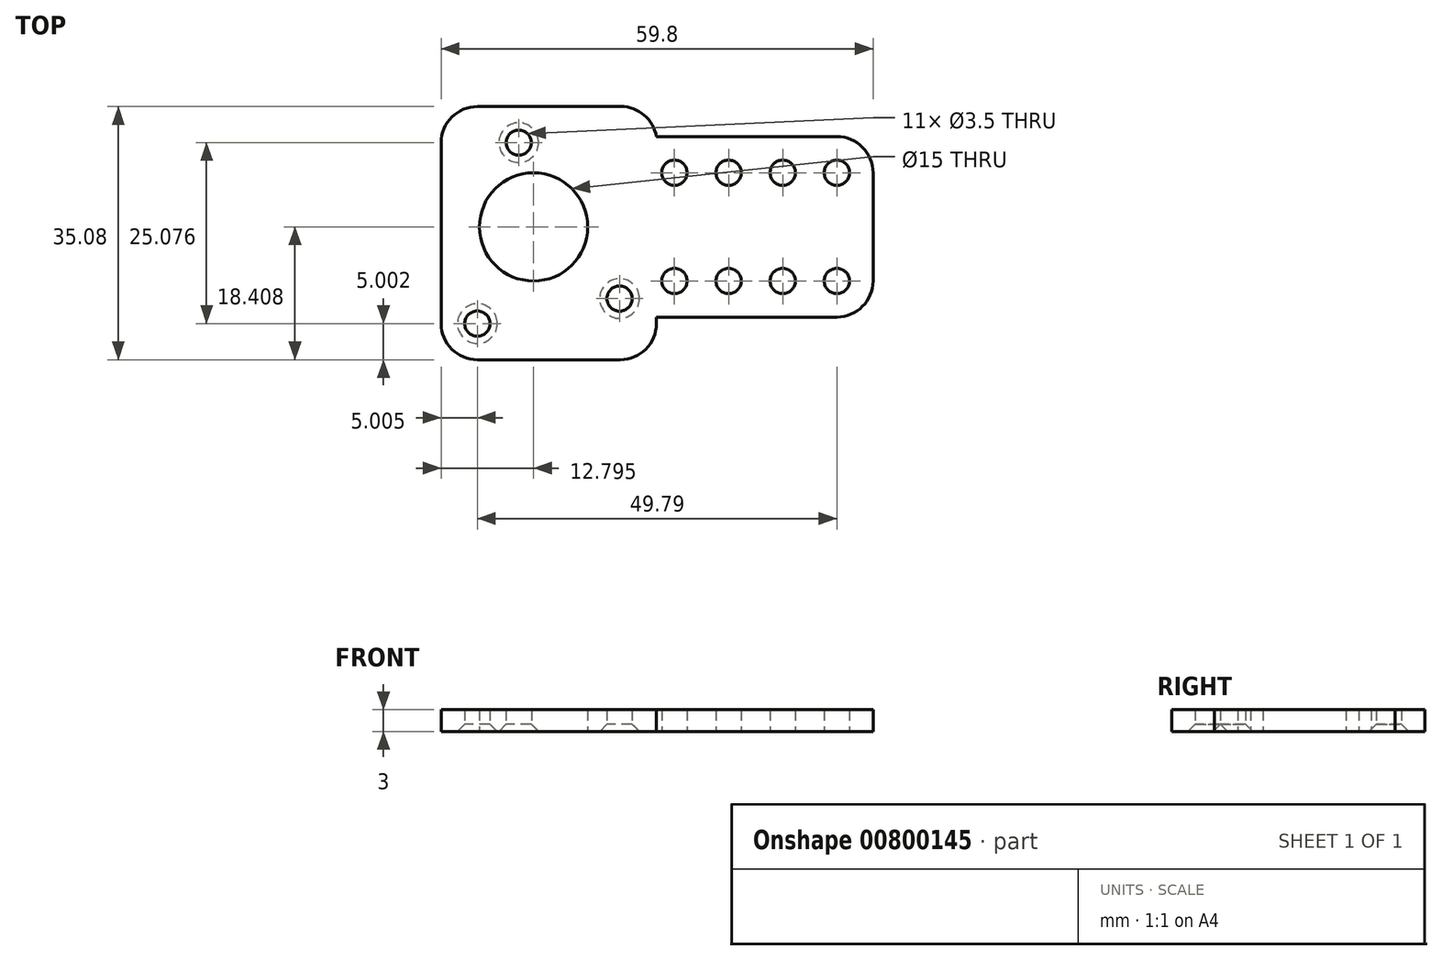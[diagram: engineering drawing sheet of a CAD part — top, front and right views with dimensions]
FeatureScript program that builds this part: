
annotation { "Feature Type Name" : "Feature", "Feature Type Description" : "" }
export const myFeature = defineFeature(function(context is Context, id is Id, definition is map)
    precondition{}
    {
        {
            var Q0;
            Q0=qCreatedBy(makeId("Top.planeOp"),FACE);
            var sketch = newSketch(context, id + "F0", { "sketchPlane" : qUnion([Q0])});
            skLineSegment(sketch, "E0.bottom", {"start": v(-29.9, 17.54) * mm, "end": v(29.9, 17.54) * mm});
            skLineSegment(sketch, "E0.top", {"start": v(-29.9, -17.54) * mm, "end": v(29.9, -17.54) * mm});
            skLineSegment(sketch, "E0.left", {"start": v(-29.9, 17.54) * mm, "end": v(-29.9, -17.54) * mm});
            skLineSegment(sketch, "E0.right", {"start": v(29.9, 17.54) * mm, "end": v(29.9, -17.54) * mm});
            skPoint(sketch, "E0.middle", {"position": v(0, 0) * mm});
            skCircle(sketch, "E1", {"center": v(-19.16, 12.54) * mm, "radius": 1.75 * mm});
            skLineSegment(sketch, "E2", {"start": v(-19.16, 12.54) * mm, "end": v(-15.05, -10.8) * mm, "construction": true});
            skLineSegment(sketch, "E3", {"start": v(-24.9, -12.54) * mm, "end": v(-5.2, -9.07) * mm, "construction": true});
            skPoint(sketch, "E4", {"position": v(-15.05, -10.8) * mm});
            skCircle(sketch, "E5", {"center": v(-5.2, -9.07) * mm, "radius": 1.75 * mm});
            skCircle(sketch, "E6.MirrorC", {"center": v(-24.9, -12.54) * mm, "radius": 1.75 * mm});
            skCircle(sketch, "E7", {"center": v(24.9, 8.37) * mm, "radius": 1.75 * mm});
            skCircle(sketch, "E8", {"center": v(24.9, -6.63) * mm, "radius": 1.75 * mm});
            skPoint(sketch, "E9", {"position": v(-17.1, 0.87) * mm});
            skLineSegment(sketch, "E10", {"start": v(24.9, 8.37) * mm, "end": v(24.9, -6.63) * mm, "construction": true});
            skPoint(sketch, "E11", {"position": v(24.9, 0.87) * mm});
            skLineSegment(sketch, "E12", {"start": v(24.9, 0.87) * mm, "end": v(-17.1, 0.87) * mm, "construction": true});
            skCircle(sketch, "E13.1.0.0", {"center": v(17.4, -6.63) * mm, "radius": 1.75 * mm});
            skLineSegment(sketch, "E13.1.0.1", {"start": v(17.4, 8.37) * mm, "end": v(17.4, -6.63) * mm, "construction": true});
            skPoint(sketch, "E13.1.0.2", {"position": v(17.4, 0.87) * mm});
            skCircle(sketch, "E13.1.0.3", {"center": v(17.4, 8.37) * mm, "radius": 1.75 * mm});
            skCircle(sketch, "E13.2.0.0", {"center": v(9.9, -6.63) * mm, "radius": 1.75 * mm});
            skLineSegment(sketch, "E13.2.0.1", {"start": v(9.9, 8.37) * mm, "end": v(9.9, -6.63) * mm, "construction": true});
            skPoint(sketch, "E13.2.0.2", {"position": v(9.9, 0.87) * mm});
            skCircle(sketch, "E13.2.0.3", {"center": v(9.9, 8.37) * mm, "radius": 1.75 * mm});
            skCircle(sketch, "E13.3.0.0", {"center": v(2.4, -6.63) * mm, "radius": 1.75 * mm});
            skLineSegment(sketch, "E13.3.0.1", {"start": v(2.4, 8.37) * mm, "end": v(2.4, -6.63) * mm, "construction": true});
            skPoint(sketch, "E13.3.0.2", {"position": v(2.4, 0.87) * mm});
            skCircle(sketch, "E13.3.0.3", {"center": v(2.4, 8.37) * mm, "radius": 1.75 * mm});
            skLineSegment(sketch, "E13.direction1", {"start": v(24.9, -6.63) * mm, "end": v(17.4, -6.63) * mm, "construction": true});
            skCircle(sketch, "E14", {"center": v(-17.1, 0.87) * mm, "radius": 7.5 * mm});
            skLineSegment(sketch, "E15", {"start": v(-0.1, 13.37) * mm, "end": v(29.9, 13.37) * mm});
            skLineSegment(sketch, "E16.MirrorCS", {"start": v(-0.1, -11.63) * mm, "end": v(29.9, -11.63) * mm});
            skLineSegment(sketch, "E17", {"start": v(-0.1, -11.63) * mm, "end": v(-0.1, -17.54) * mm});
            skLineSegment(sketch, "E18", {"start": v(-0.1, 13.37) * mm, "end": v(-0.1, 17.54) * mm});
            skPoint(sketch, "E18.endSnap0", {"position": v(0, 17.54) * mm});
            skSolve(sketch);
        }
        {
            var Q0;
            Q0=makeQuery(id+"F0.imprint","IMPRINT",FACE,{"disambiguationData":[TD([[makeQuery(id+"F0.imprint","IMPRINT",EDGE,{"derivedFrom":sQuery(id+"F0.wireOp",EDGE,"E1")}),-1.0]])]});
            extrude(context, id + "F1", {"entities" : qUnion([Q0]), "depth" : 3 * mm, "offsetDistance" : 25 * mm});
        }
        {
            var Q0;
            Q0=makeQuery(id+"F1.opExtrude","CAP_EDGE",EDGE,{"disambiguationData":[OSD([sQuery(id+"F0.wireOp",EDGE,"E1")])],"isStart":true});
            var Q1;
            Q1=makeQuery(id+"F1.opExtrude","CAP_EDGE",EDGE,{"disambiguationData":[OSD([sQuery(id+"F0.wireOp",EDGE,"E5")])],"isStart":true});
            var Q2;
            Q2=makeQuery(id+"F1.opExtrude","CAP_EDGE",EDGE,{"disambiguationData":[OSD([sQuery(id+"F0.wireOp",EDGE,"E6.MirrorC")])],"isStart":true});
            chamfer(context, id + "F2", {"entities" : qUnion([Q0, Q1, Q2]), "width" : 1 * mm, "tangentPropagation" : true});
        }
        {
            var Q0;
            Q0=makeQuery(id+"F1.opExtrude","SWEPT_EDGE",EDGE,{"disambiguationData":[OSD([sQuery(id+"F0.wireOp",EDGE,"E0.bottom"),sQuery(id+"F0.wireOp",EDGE,"E0.left")])]});
            var Q1;
            Q1=makeQuery(id+"F1.opExtrude","SWEPT_EDGE",EDGE,{"disambiguationData":[OSD([sQuery(id+"F0.wireOp",EDGE,"E0.top"),sQuery(id+"F0.wireOp",EDGE,"E0.right")])]});
            var Q2;
            Q2=makeQuery(id+"F1.opExtrude","SWEPT_EDGE",EDGE,{"disambiguationData":[OSD([sQuery(id+"F0.wireOp",EDGE,"E0.bottom"),sQuery(id+"F0.wireOp",EDGE,"E0.right")])]});
            var Q3;
            Q3=makeQuery(id+"F1.opExtrude","SWEPT_EDGE",EDGE,{"disambiguationData":[OSD([sQuery(id+"F0.wireOp",EDGE,"E0.top"),sQuery(id+"F0.wireOp",EDGE,"E0.left")])]});
            fillet(context, id + "F3", {"entities" : qUnion([Q0, Q1, Q2, Q3]), "radius" : 5 * mm, "tangentPropagation" : true, "allowEdgeOverflow" : false});
        }
    });
